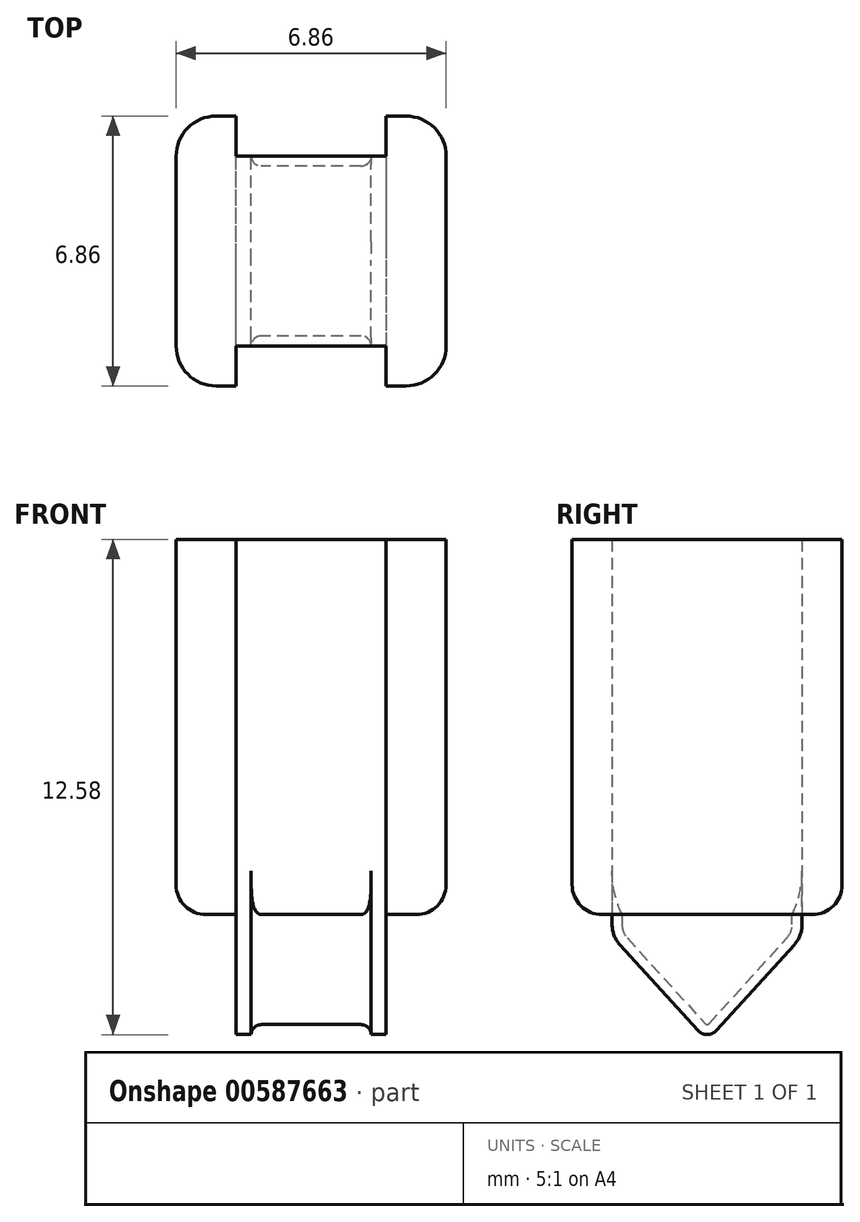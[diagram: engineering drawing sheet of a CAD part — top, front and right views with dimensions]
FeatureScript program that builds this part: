
annotation { "Feature Type Name" : "Feature", "Feature Type Description" : "" }
export const myFeature = defineFeature(function(context is Context, id is Id, definition is map)
    precondition{}
    {
        {
            var Q0;
            Q0=qCreatedBy(makeId("Top.planeOp"),FACE);
            var sketch = newSketch(context, id + "F0", { "sketchPlane" : qUnion([Q0])});
            skLineSegment(sketch, "E0", {"start": v(0, 0) * mm, "end": v(0, 2.41) * mm});
            skLineSegment(sketch, "E1", {"start": v(0, 2.41) * mm, "end": v(-1.9, 2.41) * mm});
            skLineSegment(sketch, "E2", {"start": v(-1.9, 2.41) * mm, "end": v(-1.9, 3.43) * mm});
            skLineSegment(sketch, "E3", {"start": v(-1.9, 3.43) * mm, "end": v(-3.43, 3.43) * mm});
            skLineSegment(sketch, "E4", {"start": v(-3.43, 3.43) * mm, "end": v(-3.43, -3.43) * mm});
            skLineSegment(sketch, "E5", {"start": v(-3.43, -3.43) * mm, "end": v(-1.9, -3.43) * mm});
            skLineSegment(sketch, "E6", {"start": v(-1.9, -3.43) * mm, "end": v(-1.9, 2.41) * mm});
            skLineSegment(sketch, "E7", {"start": v(0, 0) * mm, "end": v(0, -2.41) * mm});
            skLineSegment(sketch, "E8", {"start": v(0, -2.41) * mm, "end": v(-1.9, -2.41) * mm});
            skLineSegment(sketch, "E9", {"start": v(0, -2.41) * mm, "end": v(1.9, -2.41) * mm});
            skLineSegment(sketch, "E10", {"start": v(0, 2.41) * mm, "end": v(1.9, 2.41) * mm});
            skLineSegment(sketch, "E11", {"start": v(1.9, 2.41) * mm, "end": v(1.9, 3.43) * mm});
            skLineSegment(sketch, "E12", {"start": v(1.9, 3.43) * mm, "end": v(3.43, 3.43) * mm});
            skLineSegment(sketch, "E13", {"start": v(3.43, 3.43) * mm, "end": v(3.43, -3.43) * mm});
            skLineSegment(sketch, "E14", {"start": v(3.43, -3.43) * mm, "end": v(1.9, -3.43) * mm});
            skLineSegment(sketch, "E15", {"start": v(1.9, -3.43) * mm, "end": v(1.9, -2.41) * mm});
            skLineSegment(sketch, "E16", {"start": v(1.9, 2.41) * mm, "end": v(1.9, -2.41) * mm});
            skLineSegment(sketch, "E17", {"start": v(-1.9, 3.43) * mm, "end": v(1.9, 3.43) * mm, "construction": true});
            skLineSegment(sketch, "E18", {"start": v(1.9, -3.43) * mm, "end": v(-1.9, -3.43) * mm, "construction": true});
            skSolve(sketch);
        }
        {
            var Q0;
            {var subQ1=sQuery(id+"F0.wireOp",EDGE,"E2");Q0=makeQuery(id+"F0.imprint","IMPRINT",FACE,{"disambiguationData":[TD([[makeQuery(id+"F0.imprint","IMPRINT",EDGE,{"derivedFrom":subQ1}),1.0]])]});}
            var Q1;
            Q1=makeQuery(id+"F0.imprint","IMPRINT",FACE,{"disambiguationData":[TD([[makeQuery(id+"F0.imprint","IMPRINT",EDGE,{"derivedFrom":sQuery(id+"F0.wireOp",EDGE,"E0")}),1.0]])]});
            var Q2;
            Q2=makeQuery(id+"F0.imprint","IMPRINT",FACE,{"disambiguationData":[TD([[makeQuery(id+"F0.imprint","IMPRINT",EDGE,{"derivedFrom":sQuery(id+"F0.wireOp",EDGE,"E0")}),-1.0]])]});
            var Q3;
            Q3=makeQuery(id+"F0.imprint","IMPRINT",FACE,{"disambiguationData":[TD([[makeQuery(id+"F0.imprint","IMPRINT",EDGE,{"derivedFrom":sQuery(id+"F0.wireOp",EDGE,"E11")}),-1.0]])]});
            extrude(context, id + "F1", {"entities" : qUnion([Q0, Q1, Q2, Q3]), "depth" : 9.52 * mm, "offsetDistance" : 25.4 * mm});
        }
        {
            var Q0;
            Q0=makeQuery(id+"F0.imprint","IMPRINT",FACE,{"disambiguationData":[TD([[makeQuery(id+"F0.imprint","IMPRINT",EDGE,{"derivedFrom":sQuery(id+"F0.wireOp",EDGE,"E0")}),-1.0]])]});
            var Q1;
            Q1=makeQuery(id+"F0.imprint","IMPRINT",FACE,{"disambiguationData":[TD([[makeQuery(id+"F0.imprint","IMPRINT",EDGE,{"derivedFrom":sQuery(id+"F0.wireOp",EDGE,"E0")}),1.0]])]});
            extrude(context, id + "F2", {"entities" : qUnion([Q0, Q1]), "operationType" : NewBodyOperationType.ADD, "oppositeDirection" : true, "depth" : 3.05 * mm, "offsetDistance" : 25.4 * mm});
        }
        {
            var Q0;
            Q0=qCreatedBy(makeId("Right.planeOp"),FACE);
            var sketch = newSketch(context, id + "F3", { "sketchPlane" : qUnion([Q0])});
            skLineSegment(sketch, "E19.0", {"start": v(2.41, -3.05) * mm, "end": v(2.41, 0) * mm, "construction": true});
            skLineSegment(sketch, "E19.1", {"start": v(-2.41, -3.05) * mm, "end": v(-2.41, 0) * mm, "construction": true});
            skLineSegment(sketch, "E19.2", {"start": v(2.41, -3.05) * mm, "end": v(-2.41, -3.05) * mm, "construction": true});
            skLineSegment(sketch, "E19.3", {"start": v(2.41, 0) * mm, "end": v(-2.41, 0) * mm, "construction": true});
            skLineSegment(sketch, "E20", {"start": v(-2.41, -0.25) * mm, "end": v(2.41, -0.25) * mm, "construction": true});
            skLineSegment(sketch, "E21", {"start": v(0, -3.05) * mm, "end": v(0, -2.73) * mm, "construction": true});
            skPoint(sketch, "E21.endSnap0", {"position": v(0, -3.05) * mm});
            skLineSegment(sketch, "E22", {"start": v(0, -2.73) * mm, "end": v(0, -0.25) * mm, "construction": true});
            skArc(sketch, "E23", {"start": v(-0.23, -2.94) * mm, "mid": v(0, -3.05) * mm, "end": v(0.23, -2.94) * mm});
            skArc(sketch, "E24", {"start": v(-2.41, -0.25) * mm, "mid": v(-2.36, -0.53) * mm, "end": v(-2.21, -0.77) * mm});
            skArc(sketch, "E25", {"start": v(2.21, -0.77) * mm, "mid": v(2.36, -0.53) * mm, "end": v(2.41, -0.25) * mm});
            skLineSegment(sketch, "E26", {"start": v(-2.21, -0.77) * mm, "end": v(-0.23, -2.94) * mm});
            skLineSegment(sketch, "E27", {"start": v(0.23, -2.94) * mm, "end": v(2.21, -0.77) * mm});
            skLineSegment(sketch, "E28", {"start": v(2.41, -0.25) * mm, "end": v(2.41, 0) * mm});
            skLineSegment(sketch, "E29", {"start": v(-2.41, -0.25) * mm, "end": v(-2.41, 0) * mm});
            skLineSegment(sketch, "E30", {"start": v(-2.41, -0.25) * mm, "end": v(-2.41, -3.05) * mm});
            skLineSegment(sketch, "E31", {"start": v(2.41, -0.25) * mm, "end": v(2.41, -3.05) * mm});
            skLineSegment(sketch, "E32", {"start": v(2.41, -3.05) * mm, "end": v(0, -3.05) * mm});
            skLineSegment(sketch, "E33", {"start": v(0, -3.05) * mm, "end": v(-2.41, -3.05) * mm});
            skSolve(sketch);
        }
        {
            var Q0;
            Q0 = qSketchRegion(id + "F3", true);
            extrude(context, id + "F4", {"entities" : qUnion([Q0]), "operationType" : NewBodyOperationType.REMOVE, "endBound" : BoundingType.SYMMETRIC, "oppositeDirection" : true, "depth" : 6.35 * mm, "offsetDistance" : 25.4 * mm});
        }
        {
            var Q0;
            Q0=qCreatedBy(makeId("Top.planeOp"),FACE);
            var sketch = newSketch(context, id + "F5", { "sketchPlane" : qUnion([Q0])});
            skCircle(sketch, "E34", {"center": v(-1.27, -2.41) * mm, "radius": 0.25 * mm});
            skCircle(sketch, "E35", {"center": v(-0.64, -2.41) * mm, "radius": 0.25 * mm});
            skCircle(sketch, "E36", {"center": v(0, -2.41) * mm, "radius": 0.25 * mm});
            skLineSegment(sketch, "E37", {"start": v(-0.64, -2.41) * mm, "end": v(0, -2.41) * mm, "construction": true});
            skLineSegment(sketch, "E38", {"start": v(-0.64, -2.41) * mm, "end": v(-1.27, -2.41) * mm, "construction": true});
            skCircle(sketch, "E39", {"center": v(0.64, -2.41) * mm, "radius": 0.25 * mm});
            skCircle(sketch, "E40", {"center": v(1.27, -2.41) * mm, "radius": 0.25 * mm});
            skLineSegment(sketch, "E41", {"start": v(0, -2.41) * mm, "end": v(0.64, -2.41) * mm, "construction": true});
            skLineSegment(sketch, "E42", {"start": v(0.64, -2.41) * mm, "end": v(1.27, -2.41) * mm, "construction": true});
            skLineSegment(sketch, "E43", {"start": v(-1.27, -2.67) * mm, "end": v(1.27, -2.67) * mm});
            skLineSegment(sketch, "E44", {"start": v(1.27, -2.16) * mm, "end": v(-1.27, -2.16) * mm});
            skSolve(sketch);
        }
        {
            var Q0;
            Q0=qCreatedBy(makeId("Right.planeOp"),FACE);
            var sketch = newSketch(context, id + "F6", { "sketchPlane" : qUnion([Q0])});
            skArc(sketch, "E45.0.0", {"start": v(0.23, -2.94) * mm, "mid": v(0, -3.05) * mm, "end": v(-0.23, -2.94) * mm});
            skLineSegment(sketch, "E45.0.1", {"start": v(-0.23, -2.94) * mm, "end": v(-2.21, -0.77) * mm});
            skArc(sketch, "E45.0.2", {"start": v(-2.21, -0.77) * mm, "mid": v(-2.36, -0.53) * mm, "end": v(-2.41, -0.25) * mm});
            skLineSegment(sketch, "E45.0.3", {"start": v(-2.41, -0.25) * mm, "end": v(-2.41, 0) * mm});
            skLineSegment(sketch, "E45.0.4", {"start": v(-2.41, 0) * mm, "end": v(2.41, 0) * mm, "construction": true});
            skLineSegment(sketch, "E45.0.5", {"start": v(2.41, 0) * mm, "end": v(2.41, -0.25) * mm});
            skArc(sketch, "E45.0.6", {"start": v(2.41, -0.25) * mm, "mid": v(2.36, -0.53) * mm, "end": v(2.21, -0.77) * mm});
            skLineSegment(sketch, "E45.0.7", {"start": v(2.21, -0.77) * mm, "end": v(0.23, -2.94) * mm});
            skSolve(sketch);
        }
        {
            var Q0;
            Q0 = qSketchRegion(id + "F5", true);
            var Q1;
            Q1 = qConstructionFilter(qBodyType(qCreatedBy(id + "F6" ,EDGE), BodyType.WIRE), ConstructionObject.NO);
            sweep(context, id + "F7", {"operationType" : NewBodyOperationType.REMOVE, "profiles" : qUnion([Q0]), "path" : qUnion([Q1])});
        }
        {
            var Q0;
            Q0=makeQuery(id+"F1.opExtrude","SWEPT_EDGE",EDGE,{"disambiguationData":[OSD([sQuery(id+"F0.wireOp",EDGE,"E13"),sQuery(id+"F0.wireOp",EDGE,"E14")])]});
            var Q1;
            Q1=makeQuery(id+"F1.opExtrude","SWEPT_EDGE",EDGE,{"disambiguationData":[OSD([sQuery(id+"F0.wireOp",EDGE,"E4"),sQuery(id+"F0.wireOp",EDGE,"E5")])]});
            var Q2;
            Q2=makeQuery(id+"F1.opExtrude","SWEPT_EDGE",EDGE,{"disambiguationData":[OSD([sQuery(id+"F0.wireOp",EDGE,"E3"),sQuery(id+"F0.wireOp",EDGE,"E4")])]});
            var Q3;
            Q3=makeQuery(id+"F1.opExtrude","SWEPT_EDGE",EDGE,{"disambiguationData":[OSD([sQuery(id+"F0.wireOp",EDGE,"E12"),sQuery(id+"F0.wireOp",EDGE,"E13")])]});
            fillet(context, id + "F8", {"entities" : qUnion([Q0, Q1, Q2, Q3]), "radius" : 1.02 * mm, "tangentPropagation" : true, "allowEdgeOverflow" : false});
        }
        {
            var Q0;
            Q0=makeQuery(id+"F1.opExtrude","CAP_EDGE",EDGE,{"disambiguationData":[OSD([sQuery(id+"F0.wireOp",EDGE,"E13")])],"isStart":true});
            var Q1;
            {var subQ0=sQuery(id+"F0.wireOp",EDGE,"E12");var subQ1=sQuery(id+"F0.wireOp",EDGE,"E11");var subQ2=sQuery(id+"F0.wireOp",EDGE,"E9");var subQ3=sQuery(id+"F0.wireOp",EDGE,"E8");var subQ4=sQuery(id+"F0.wireOp",EDGE,"E10");var subQ5=sQuery(id+"F0.wireOp",EDGE,"E1");var subQ6=sQuery(id+"F0.wireOp",EDGE,"E15");var subQ7=sQuery(id+"F0.wireOp",EDGE,"E13");var subQ8=sQuery(id+"F0.wireOp",EDGE,"E14");Q1=makeQuery(id+"F8.opFillet","BLEND_EDGE",EDGE,{"blendedFrom":[makeQuery(id+"F1.opExtrude","SWEPT_EDGE",EDGE,{"disambiguationData":[OSD([subQ0,subQ7])]}),makeQuery(id+"F2.boolean.opBoolean","SPLIT",FACE,{"disambiguationData":[TD([makeQuery(id+"F1.opExtrude","SWEPT_FACE",FACE,{"disambiguationData":[OSD([subQ1])]})])],"derivedFrom":makeQuery(id+"F1.opExtrude","CAP_FACE",FACE,{"disambiguationData":[OSD([subQ5,sQuery(id+"F0.wireOp",EDGE,"E2"),sQuery(id+"F0.wireOp",EDGE,"E3"),sQuery(id+"F0.wireOp",EDGE,"E4"),sQuery(id+"F0.wireOp",EDGE,"E5"),sQuery(id+"F0.wireOp",EDGE,"E6"),subQ3,subQ2,subQ4,subQ1,subQ0,subQ7,subQ8,subQ6])],"isStart":true})})],"blendedInto":[makeQuery(id+"F2.boolean.opBoolean","SPLIT",FACE,{"disambiguationData":[TD([makeQuery(id+"F1.opExtrude","SWEPT_FACE",FACE,{"disambiguationData":[OSD([subQ1])]})])],"derivedFrom":makeQuery(id+"F1.opExtrude","CAP_FACE",FACE,{"disambiguationData":[OSD([subQ5,sQuery(id+"F0.wireOp",EDGE,"E2"),sQuery(id+"F0.wireOp",EDGE,"E3"),sQuery(id+"F0.wireOp",EDGE,"E4"),sQuery(id+"F0.wireOp",EDGE,"E5"),sQuery(id+"F0.wireOp",EDGE,"E6"),subQ3,subQ2,subQ4,subQ1,subQ0,subQ7,subQ8,subQ6])],"isStart":true})})]});}
            var Q2;
            Q2=makeQuery(id+"F1.opExtrude","CAP_EDGE",EDGE,{"disambiguationData":[OSD([sQuery(id+"F0.wireOp",EDGE,"E12")])],"isStart":true});
            var Q3;
            {var subQ0=sQuery(id+"F0.wireOp",EDGE,"E12");var subQ1=sQuery(id+"F0.wireOp",EDGE,"E11");var subQ2=sQuery(id+"F0.wireOp",EDGE,"E9");var subQ3=sQuery(id+"F0.wireOp",EDGE,"E8");var subQ4=sQuery(id+"F0.wireOp",EDGE,"E10");var subQ5=sQuery(id+"F0.wireOp",EDGE,"E1");var subQ6=sQuery(id+"F0.wireOp",EDGE,"E15");var subQ7=sQuery(id+"F0.wireOp",EDGE,"E13");var subQ8=sQuery(id+"F0.wireOp",EDGE,"E14");Q3=makeQuery(id+"F8.opFillet","BLEND_EDGE",EDGE,{"blendedFrom":[makeQuery(id+"F1.opExtrude","SWEPT_EDGE",EDGE,{"disambiguationData":[OSD([subQ7,subQ8])]}),makeQuery(id+"F2.boolean.opBoolean","SPLIT",FACE,{"disambiguationData":[TD([makeQuery(id+"F1.opExtrude","SWEPT_FACE",FACE,{"disambiguationData":[OSD([subQ1])]})])],"derivedFrom":makeQuery(id+"F1.opExtrude","CAP_FACE",FACE,{"disambiguationData":[OSD([subQ5,sQuery(id+"F0.wireOp",EDGE,"E2"),sQuery(id+"F0.wireOp",EDGE,"E3"),sQuery(id+"F0.wireOp",EDGE,"E4"),sQuery(id+"F0.wireOp",EDGE,"E5"),sQuery(id+"F0.wireOp",EDGE,"E6"),subQ3,subQ2,subQ4,subQ1,subQ0,subQ7,subQ8,subQ6])],"isStart":true})})],"blendedInto":[makeQuery(id+"F2.boolean.opBoolean","SPLIT",FACE,{"disambiguationData":[TD([makeQuery(id+"F1.opExtrude","SWEPT_FACE",FACE,{"disambiguationData":[OSD([subQ1])]})])],"derivedFrom":makeQuery(id+"F1.opExtrude","CAP_FACE",FACE,{"disambiguationData":[OSD([subQ5,sQuery(id+"F0.wireOp",EDGE,"E2"),sQuery(id+"F0.wireOp",EDGE,"E3"),sQuery(id+"F0.wireOp",EDGE,"E4"),sQuery(id+"F0.wireOp",EDGE,"E5"),sQuery(id+"F0.wireOp",EDGE,"E6"),subQ3,subQ2,subQ4,subQ1,subQ0,subQ7,subQ8,subQ6])],"isStart":true})})]});}
            var Q4;
            Q4=makeQuery(id+"F1.opExtrude","CAP_EDGE",EDGE,{"disambiguationData":[OSD([sQuery(id+"F0.wireOp",EDGE,"E14")])],"isStart":true});
            var Q5;
            {var subQ0=sQuery(id+"F0.wireOp",EDGE,"E4");var subQ1=sQuery(id+"F0.wireOp",EDGE,"E3");var subQ2=sQuery(id+"F0.wireOp",EDGE,"E2");var subQ3=sQuery(id+"F0.wireOp",EDGE,"E10");var subQ4=sQuery(id+"F0.wireOp",EDGE,"E1");var subQ5=sQuery(id+"F0.wireOp",EDGE,"E5");var subQ6=sQuery(id+"F0.wireOp",EDGE,"E6");var subQ7=sQuery(id+"F0.wireOp",EDGE,"E9");var subQ8=sQuery(id+"F0.wireOp",EDGE,"E8");Q5=makeQuery(id+"F8.opFillet","BLEND_EDGE",EDGE,{"blendedFrom":[makeQuery(id+"F1.opExtrude","SWEPT_EDGE",EDGE,{"disambiguationData":[OSD([subQ1,subQ0])]}),makeQuery(id+"F2.boolean.opBoolean","SPLIT",FACE,{"disambiguationData":[TD([makeQuery(id+"F1.opExtrude","SWEPT_FACE",FACE,{"disambiguationData":[OSD([subQ2])]})])],"derivedFrom":makeQuery(id+"F1.opExtrude","CAP_FACE",FACE,{"disambiguationData":[OSD([subQ4,subQ2,subQ1,subQ0,subQ5,subQ6,subQ8,subQ7,subQ3,sQuery(id+"F0.wireOp",EDGE,"E11"),sQuery(id+"F0.wireOp",EDGE,"E12"),sQuery(id+"F0.wireOp",EDGE,"E13"),sQuery(id+"F0.wireOp",EDGE,"E14"),sQuery(id+"F0.wireOp",EDGE,"E15")])],"isStart":true})})],"blendedInto":[makeQuery(id+"F2.boolean.opBoolean","SPLIT",FACE,{"disambiguationData":[TD([makeQuery(id+"F1.opExtrude","SWEPT_FACE",FACE,{"disambiguationData":[OSD([subQ2])]})])],"derivedFrom":makeQuery(id+"F1.opExtrude","CAP_FACE",FACE,{"disambiguationData":[OSD([subQ4,subQ2,subQ1,subQ0,subQ5,subQ6,subQ8,subQ7,subQ3,sQuery(id+"F0.wireOp",EDGE,"E11"),sQuery(id+"F0.wireOp",EDGE,"E12"),sQuery(id+"F0.wireOp",EDGE,"E13"),sQuery(id+"F0.wireOp",EDGE,"E14"),sQuery(id+"F0.wireOp",EDGE,"E15")])],"isStart":true})})]});}
            var Q6;
            Q6=makeQuery(id+"F1.opExtrude","CAP_EDGE",EDGE,{"disambiguationData":[OSD([sQuery(id+"F0.wireOp",EDGE,"E3")])],"isStart":true});
            var Q7;
            Q7=makeQuery(id+"F1.opExtrude","CAP_EDGE",EDGE,{"disambiguationData":[OSD([sQuery(id+"F0.wireOp",EDGE,"E4")])],"isStart":true});
            var Q8;
            Q8=makeQuery(id+"F1.opExtrude","CAP_EDGE",EDGE,{"disambiguationData":[OSD([sQuery(id+"F0.wireOp",EDGE,"E5")])],"isStart":true});
            var Q9;
            {var subQ0=sQuery(id+"F0.wireOp",EDGE,"E4");var subQ1=sQuery(id+"F0.wireOp",EDGE,"E3");var subQ2=sQuery(id+"F0.wireOp",EDGE,"E2");var subQ3=sQuery(id+"F0.wireOp",EDGE,"E10");var subQ4=sQuery(id+"F0.wireOp",EDGE,"E1");var subQ5=sQuery(id+"F0.wireOp",EDGE,"E5");var subQ6=sQuery(id+"F0.wireOp",EDGE,"E6");var subQ7=sQuery(id+"F0.wireOp",EDGE,"E9");var subQ8=sQuery(id+"F0.wireOp",EDGE,"E8");Q9=makeQuery(id+"F8.opFillet","BLEND_EDGE",EDGE,{"blendedFrom":[makeQuery(id+"F1.opExtrude","SWEPT_EDGE",EDGE,{"disambiguationData":[OSD([subQ0,subQ5])]}),makeQuery(id+"F2.boolean.opBoolean","SPLIT",FACE,{"disambiguationData":[TD([makeQuery(id+"F1.opExtrude","SWEPT_FACE",FACE,{"disambiguationData":[OSD([subQ2])]})])],"derivedFrom":makeQuery(id+"F1.opExtrude","CAP_FACE",FACE,{"disambiguationData":[OSD([subQ4,subQ2,subQ1,subQ0,subQ5,subQ6,subQ8,subQ7,subQ3,sQuery(id+"F0.wireOp",EDGE,"E11"),sQuery(id+"F0.wireOp",EDGE,"E12"),sQuery(id+"F0.wireOp",EDGE,"E13"),sQuery(id+"F0.wireOp",EDGE,"E14"),sQuery(id+"F0.wireOp",EDGE,"E15")])],"isStart":true})})],"blendedInto":[makeQuery(id+"F2.boolean.opBoolean","SPLIT",FACE,{"disambiguationData":[TD([makeQuery(id+"F1.opExtrude","SWEPT_FACE",FACE,{"disambiguationData":[OSD([subQ2])]})])],"derivedFrom":makeQuery(id+"F1.opExtrude","CAP_FACE",FACE,{"disambiguationData":[OSD([subQ4,subQ2,subQ1,subQ0,subQ5,subQ6,subQ8,subQ7,subQ3,sQuery(id+"F0.wireOp",EDGE,"E11"),sQuery(id+"F0.wireOp",EDGE,"E12"),sQuery(id+"F0.wireOp",EDGE,"E13"),sQuery(id+"F0.wireOp",EDGE,"E14"),sQuery(id+"F0.wireOp",EDGE,"E15")])],"isStart":true})})]});}
            fillet(context, id + "F9", {"entities" : qUnion([Q0, Q1, Q2, Q3, Q4, Q5, Q6, Q7, Q8, Q9]), "radius" : 0.76 * mm, "tangentPropagation" : true, "allowEdgeOverflow" : false});
        }
        {
            var Q0;
            {var subQ0=sQuery(id+"F0.wireOp",EDGE,"E9");var subQ1=sQuery(id+"F0.wireOp",EDGE,"E8");Q0=makeQuery(id+"F7.boolean.opBoolean","INTERSECT",EDGE,{"derivedFrom":[makeQuery(id+"F2.boolean.opBoolean","MERGE",FACE,{"derivedFrom":[makeQuery(id+"F1.opExtrude","SWEPT_FACE",FACE,{"disambiguationData":[OSD([subQ1,subQ0])]}),makeQuery(id+"F2.opExtrude","SWEPT_FACE",FACE,{"disambiguationData":[OSD([subQ1,subQ0])]})]}),makeQuery(id+"F7.opSweep","CAP_FACE",FACE,{"disambiguationData":[OSD([sQuery(id+"F5.wireOp",EDGE,"E34"),sQuery(id+"F5.wireOp",EDGE,"E40"),sQuery(id+"F5.wireOp",EDGE,"E43"),sQuery(id+"F5.wireOp",EDGE,"E44"),sQuery(id+"F6.wireOp",VERTEX,"E45.0.3.end")])],"isStart":true})]});}
            var Q1;
            {var subQ0=sQuery(id+"F0.wireOp",EDGE,"E10");var subQ1=sQuery(id+"F0.wireOp",EDGE,"E1");Q1=makeQuery(id+"F7.boolean.opBoolean","INTERSECT",EDGE,{"derivedFrom":[makeQuery(id+"F2.boolean.opBoolean","MERGE",FACE,{"derivedFrom":[makeQuery(id+"F1.opExtrude","SWEPT_FACE",FACE,{"disambiguationData":[OSD([subQ1,subQ0])]}),makeQuery(id+"F2.opExtrude","SWEPT_FACE",FACE,{"disambiguationData":[OSD([subQ1,subQ0])]})]}),makeQuery(id+"F7.opSweep","CAP_FACE",FACE,{"disambiguationData":[OSD([sQuery(id+"F5.wireOp",EDGE,"E34"),sQuery(id+"F5.wireOp",EDGE,"E40"),sQuery(id+"F5.wireOp",EDGE,"E43"),sQuery(id+"F5.wireOp",EDGE,"E44"),sQuery(id+"F6.wireOp",VERTEX,"E45.0.5.start")])],"isStart":false})]});}
            fillet(context, id + "F10", {"entities" : qUnion([Q0, Q1]), "radius" : 2.54 * mm, "tangentPropagation" : true, "allowEdgeOverflow" : false});
        }
    });
